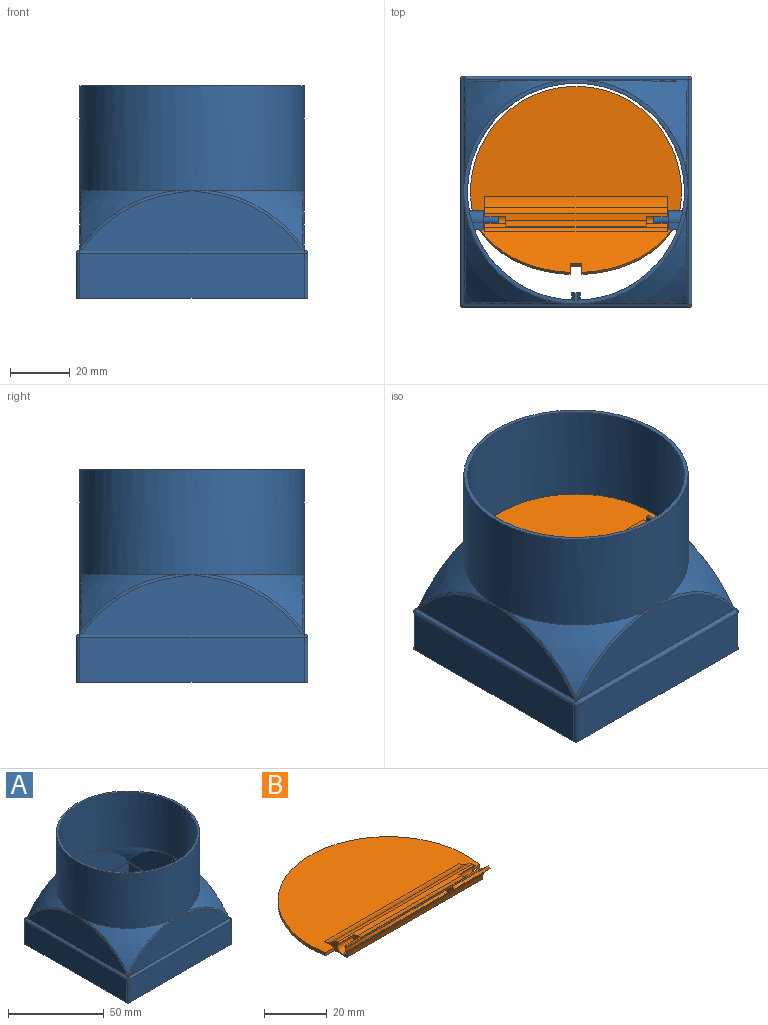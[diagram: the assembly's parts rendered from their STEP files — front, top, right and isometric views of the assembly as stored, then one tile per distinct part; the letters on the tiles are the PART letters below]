
ASSEMBLY  parts=2 mates=1
PART A: 82 faces, bbox 103.8x103.8x71.2 mm
  f0: plane 73.83x20.2mm, normal (0,1,0), area 1007.4mm2, adj f1,f2,f3,f4,f5
  f1: plane 75.11x75.11mm, normal (0,0,1), area 15.2mm2, adj f0,f2,f5,f6,f7,f8,f9,f10
  f2: torus R=44.59mm, axis (0,-1,0), area 40.5mm2, adj f0,f1,f3,f17,f19
  f3: bspline ~6.37x1mm, area 2mm2, adj f0,f2,f20
  f4: bspline ~6.37x1mm, area 2mm2, adj f0,f5,f20
  f5: torus R=44.59mm, axis (0,-1,0), area 40.5mm2, adj f0,f1,f4,f16,f21
  f6: cylinder r=1.2mm len=75.1mm, axis (0,-1,0), area 141.6mm2, adj f1,f22,f23,f24
  f7: cylinder r=1.2mm len=75.1mm, axis (1,0,0), area 141.6mm2, adj f1,f22,f25,f26
  f8: cylinder r=1.2mm len=75.1mm, axis (0,1,0), area 141.6mm2, adj f1,f26,f27,f28
  f9: cylinder r=1.2mm len=75.1mm, axis (-1,0,0), area 141.6mm2, adj f1,f23,f28,f29
  f10: torus R=44.59mm, axis (-1,0,0), area 40.5mm2, adj f1,f11,f18,f30,f31
  f11: torus R=44.59mm, axis (0,-1,0), area 40.5mm2, adj f1,f10,f12,f30,f32
  f12: plane 73.83x20.19mm, normal (0,-1,0), area 1007.4mm2, adj f1,f11,f13,f32,f33
  f13: torus R=44.59mm, axis (0,-1,0), area 40.5mm2, adj f1,f12,f14,f33,f34
  f14: torus R=44.59mm, axis (-1,0,0), area 40.5mm2, adj f1,f13,f15,f34,f35
  f15: plane 73.83x20.2mm, normal (1,0,0), area 1007.4mm2, adj f1,f14,f16,f35,f36
  f16: torus R=44.59mm, axis (-1,0,0), area 40.5mm2, adj f1,f5,f15,f21,f36
  f17: torus R=44.59mm, axis (-1,0,0), area 40.5mm2, adj f1,f2,f18,f19,f37
  f18: plane 73.83x20.19mm, normal (-1,0,0), area 1007.4mm2, adj f1,f10,f17,f31,f37
  f19: sphere r=58.7mm, area 397.7mm2, adj f2,f17,f20
  f20: cylinder r=37.5mm len=75mm, axis (0,0,-1), area 8246.7mm2, adj f3,f4,f19,f21,f30,f31,f32,f33
  f21: sphere r=58.7mm, area 397.7mm2, adj f5,f16,f20
  f22: sphere r=1.2mm, area 1.4mm2, adj f6,f7,f39
  f23: sphere r=1.2mm, area 2.3mm2, adj f6,f9,f40
  f24: plane 75.1x14.8mm, normal (1,0,0), area 1111.5mm2, adj f6,f39,f40,f41
  f25: plane 75.1x14.8mm, normal (0,1,0), area 1111.5mm2, adj f7,f39,f41,f42
  f26: sphere r=1.2mm, area 3.1mm2, adj f7,f8,f42
  f27: plane 75.1x14.8mm, normal (-1,0,0), area 1111.5mm2, adj f8,f41,f42,f43
  f28: sphere r=1.2mm, area 2.3mm2, adj f8,f9,f43
  f29: plane 75.1x14.8mm, normal (0,-1,0), area 1111.5mm2, adj f9,f40,f41,f43
  f30: sphere r=58.7mm, area 397.7mm2, adj f10,f11,f20
  f31: bspline ~9.4x1.25mm, area 2mm2, adj f10,f18,f20
  f32: bspline ~9.4x1.25mm, area 2mm2, adj f11,f12,f20
  f33: bspline ~9.4x1.25mm, area 2mm2, adj f12,f13,f20
  f34: sphere r=58.7mm, area 397.7mm2, adj f13,f14,f20
  f35: bspline ~6.37x1mm, area 2mm2, adj f14,f15,f20
  f36: bspline ~6.37x1mm, area 2mm2, adj f15,f16,f20
  f37: bspline ~9.4x1.25mm, area 2mm2, adj f17,f18,f20
  f38: plane 75x75mm, normal (0,0,1), area 292.1mm2, adj f20,f44,f45,f46,f47
  f39: cylinder r=1.2mm len=14.8mm, axis (0,0,-1), area 27.9mm2, adj f22,f24,f25,f41
  f40: cylinder r=1.2mm len=14.8mm, axis (0,0,1), area 27.9mm2, adj f23,f24,f29,f41
  f41: plane 77.5x77.5mm, normal (0,0,-1), area 380mm2, adj f24,f25,f27,f29,f39,f40,f42,f43
  f42: cylinder r=1.2mm len=14.8mm, axis (0,0,1), area 27.9mm2, adj f25,f26,f27,f41
  f43: cylinder r=1.2mm len=14.8mm, axis (0,0,-1), area 27.9mm2, adj f27,f28,f29,f41
  f44: cylinder r=36.25mm len=72.5mm, axis (0,0,-1), area 7901.8mm2, adj f38,f45,f47,f52,f53,f54,f55
  f45: plane 35.01x2.53mm, normal (1,0,0.03), area 88mm2, adj f38,f44,f46,f56
  f46: plane 35x3mm, normal (0,1,0), area 70mm2, adj f38,f45,f47,f56
  f47: plane 35.01x2.53mm, normal (-1,0,0.03), area 88mm2, adj f38,f44,f46,f56
  f48: plane 75x14.5mm, normal (1,0,0), area 1087.5mm2, adj f41,f49,f51,f57
  f49: plane 75x14.5mm, normal (0,1,0), area 1087.5mm2, adj f41,f48,f50,f57
  f50: plane 75x14.5mm, normal (-1,0,0), area 1087.5mm2, adj f41,f49,f51,f57
  f51: plane 75x14.5mm, normal (0,-1,0), area 1087.5mm2, adj f41,f48,f50,f57
  f52: sphere r=56.13mm, area 420.3mm2, adj f44,f56,f58,f59
  f53: sphere r=56.13mm, area 420.3mm2, adj f44,f56,f58,f60
  f54: sphere r=56.13mm, area 420.3mm2, adj f44,f60,f61
  f55: sphere r=56.13mm, area 420.3mm2, adj f44,f59,f61
  f56: plane 3x2.53mm, normal (0,0,-1), area 7.6mm2, adj f45,f46,f47,f52,f53
  f57: plane 75x75mm, normal (0,0,-1), area 15mm2, adj f48,f49,f50,f51,f62,f63,f64,f65
  f58: plane 72.5x20.3mm, normal (0,1,0), area 1044.9mm2, adj f52,f53,f59,f60,f65
  f59: plane 72.5x20.3mm, normal (1,0,0), area 1044.9mm2, adj f52,f55,f58,f61,f64
  f60: plane 72.5x20.3mm, normal (-1,0,0), area 1044.9mm2, adj f53,f54,f58,f61,f62
  f61: plane 72.5x20.3mm, normal (0,-1,0), area 1044.9mm2, adj f54,f55,f59,f60,f63
  f62: cylinder r=1.2mm len=74.9mm, axis (0,1,0), area 138.9mm2, adj f57,f60,f63,f65
  f63: cylinder r=1.2mm len=74.9mm, axis (1,0,0), area 138.9mm2, adj f57,f61,f62,f64
  f64: cylinder r=1.2mm len=74.9mm, axis (0,-1,0), area 138.9mm2, adj f57,f59,f63,f65
  f65: cylinder r=1.2mm len=74.9mm, axis (-1,0,0), area 138.9mm2, adj f57,f58,f62,f64
  f66: cylinder r=36.25mm len=8.2mm, axis (0,0,-1), area 38.8mm2, adj f67,f68,f69,f70
  f67: cylinder r=3.1mm len=6.2mm, axis (-1,0,0), area 62.1mm2, adj f66,f68,f70,f71
  f68: plane 5.1x2.99mm, normal (0,-1,0), area 15.2mm2, adj f66,f67,f69,f71
  f69: plane 3.81x2.5mm, normal (0,0,1), area 8.5mm2, adj f66,f68,f70,f71
  f70: plane 3.81x2.06mm, normal (0,1,0), area 7.9mm2, adj f66,f67,f69,f71
  f71: plane 8.2x6.2mm, normal (1,0,0), area 29.6mm2, adj f67,f68,f69,f70,f72
  f72: cylinder r=1.56mm len=5mm, axis (-1,0,0), area 49mm2, adj f71,f73
  f73: plane 3.12x3.12mm, normal (1,0,0), area 7.6mm2, adj f72
  f74: cylinder r=36.25mm len=8.2mm, axis (0,0,-1), area 38.8mm2, adj f75,f76,f77,f78
  f75: cylinder r=3.1mm len=6.2mm, axis (-1,0,0), area 62.1mm2, adj f74,f76,f78,f79
  f76: plane 3.81x2.06mm, normal (0,1,0), area 7.9mm2, adj f74,f75,f77,f79
  f77: plane 3.81x2.5mm, normal (0,0,1), area 8.5mm2, adj f74,f76,f78,f79
  f78: plane 5.1x2.99mm, normal (0,-1,0), area 15.2mm2, adj f74,f75,f77,f79
  f79: plane 8.2x6.2mm, normal (-1,0,0), area 29.6mm2, adj f75,f76,f77,f78,f80
  f80: cylinder r=1.56mm len=5mm, axis (-1,0,0), area 49mm2, adj f79,f81
  f81: plane 3.12x3.12mm, normal (-1,0,0), area 7.6mm2, adj f80
PART B: 29 faces, bbox 70.5x62.9x19.1 mm
  f0: plane 61x2.13mm, normal (0,0,1), area 114.2mm2, adj f3,f5,f7,f20,f21,f22,f23,f24
  f1: plane 70.5x41.55mm, normal (0,0,1), area 2105.3mm2, adj f2,f3,f4,f5,f6,f27
  f2: cylinder r=35.25mm len=70.5mm, axis (0,0,-1), area 148.1mm2, adj f1,f4,f6,f19
  f3: plane 12.09x5.47mm, normal (1,0,0), area 16.4mm2, adj f0,f1,f4,f7,f8,f9,f15,f16
  f4: plane 4.18x1.2mm, normal (0,-1,0), area 5mm2, adj f1,f2,f3,f19
  f5: plane 12.09x5.47mm, normal (-1,0,0), area 16.4mm2, adj f0,f1,f6,f7,f8,f9,f15,f16
  f6: plane 4.18x1.2mm, normal (0,-1,0), area 5mm2, adj f1,f2,f5,f19
  f7: cylinder r=2.68mm len=61mm, axis (-1,0,0), area 140.7mm2, adj f0,f3,f5,f27
  f8: plane 61x1.26mm, normal (0,0.41,0.91), area 34.3mm2, adj f3,f5,f20,f21,f22,f23,f24,f25
  f9: plane 61x1.88mm, normal (0,-0.97,-0.25), area 118.2mm2, adj f3,f5,f26,f28
  f10: cylinder r=35.25mm len=30.34mm, axis (0,-0.71,-0.71), area 38.4mm2, adj f11,f15,f16,f17
  f11: plane 3.54x3.54mm, normal (1,0,0), area 4mm2, adj f10,f12,f15,f16
  f12: plane 4x0.71mm, normal (0,-0.71,0.71), area 4mm2, adj f11,f13,f15,f16
  f13: plane 3.54x3.54mm, normal (-1,0,0), area 4mm2, adj f12,f14,f15,f16
  f14: cylinder r=35.25mm len=30.34mm, axis (0,-0.71,-0.71), area 38.4mm2, adj f13,f15,f16,f18
  f15: plane 64.68x14.97mm, normal (0,-0.71,-0.71), area 890.3mm2, adj f3,f5,f10,f11,f12,f13,f14,f17
  f16: plane 63.77x14.26mm, normal (0,0.71,0.71), area 852.7mm2, adj f3,f5,f10,f11,f12,f13,f14,f17
  f17: plane 1.84x1.42mm, normal (0,1,0), area 2.3mm2, adj f5,f10,f15,f16
  f18: plane 1.84x1.42mm, normal (0,1,0), area 2.3mm2, adj f3,f14,f15,f16
  f19: plane 70.5x46.93mm, normal (0,0,-1), area 2721.6mm2, adj f2,f3,f4,f5,f6,f28
  f20: cylinder r=2mm len=7mm, axis (-1,0,0), area 71.8mm2, adj f0,f5,f8,f21
  f21: plane 4.11x4.06mm, normal (-1,0,0), area 12.2mm2, adj f0,f8,f20,f24
  f22: cylinder r=2mm len=7mm, axis (1,0,0), area 71.8mm2, adj f0,f3,f8,f23
  f23: plane 4.11x4.06mm, normal (1,0,0), area 12.2mm2, adj f0,f8,f22,f24
  f24: cylinder r=5mm len=47mm, axis (1,0,0), area 98.2mm2, adj f0,f8,f21,f23
  f25: cylinder r=5mm len=61mm, axis (1,0,0), area 112.1mm2, adj f3,f5,f8,f16
  f26: cylinder r=5mm len=61mm, axis (1,0,0), area 162.7mm2, adj f3,f5,f9,f15
  f27: cylinder r=5mm len=61mm, axis (-1,0,0), area 262.8mm2, adj f1,f3,f5,f7
  f28: plane 61x0.2mm, normal (0,-0.71,-0.71), area 17.3mm2, adj f3,f5,f9,f19
PLACE A t=(-0.17,1.67,0.06)mm fixed
PLACE B rot(axis=(-1,0,0),0deg) t=(-0.17,1.68,1.22)mm
MATE revolute B.f23 <-> A.f67  axis (1,0,0) through (23.33,-7.83,3.16)mm
